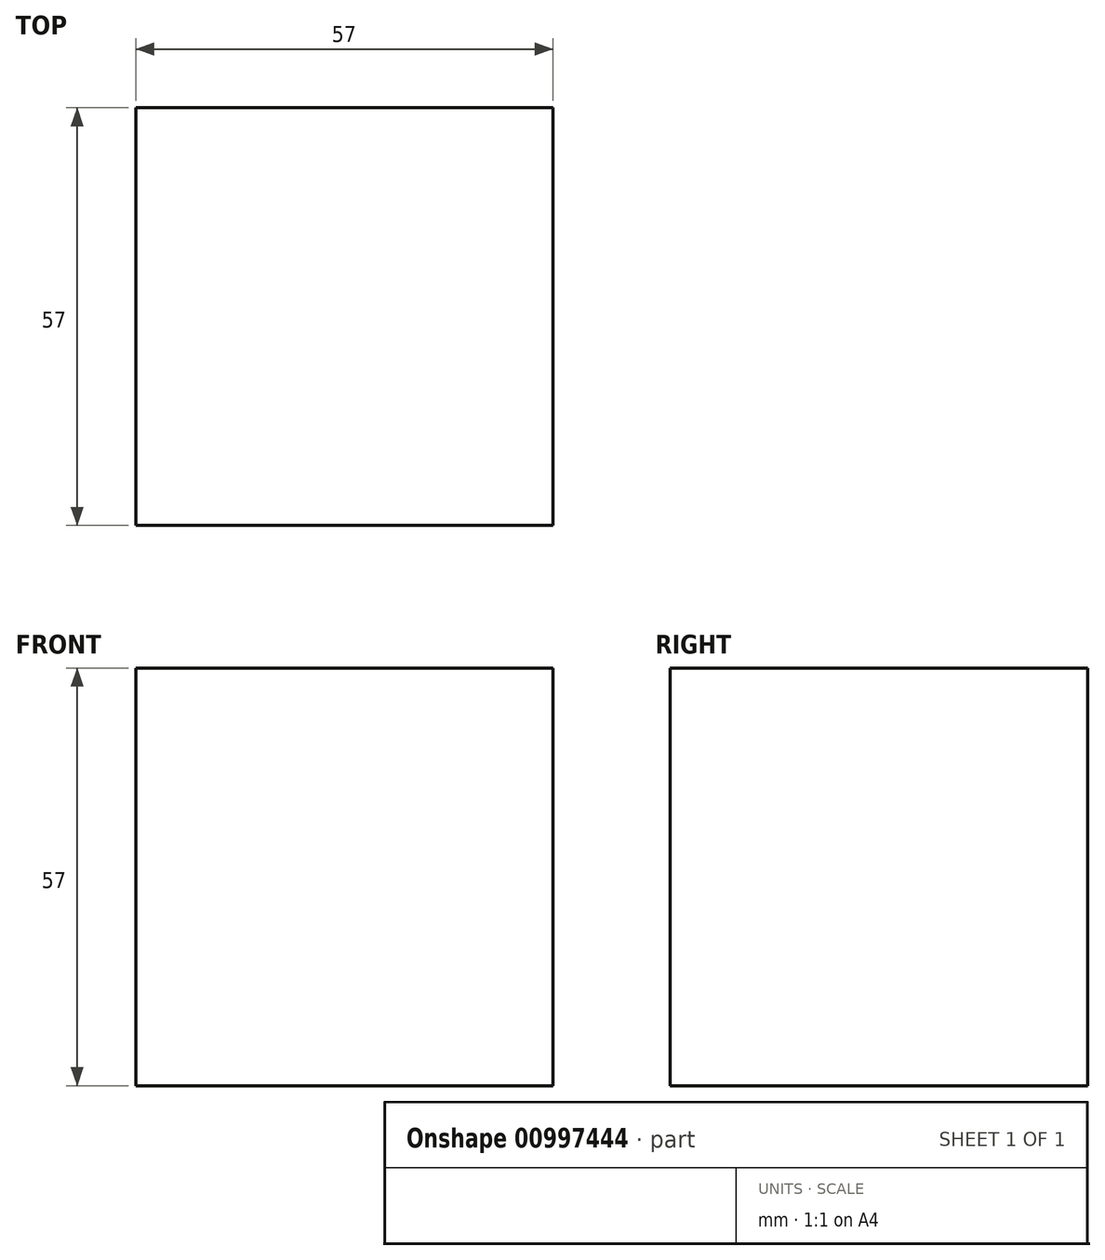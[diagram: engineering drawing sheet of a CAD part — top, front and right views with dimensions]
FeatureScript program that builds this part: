
annotation { "Feature Type Name" : "Feature", "Feature Type Description" : "" }
export const myFeature = defineFeature(function(context is Context, id is Id, definition is map)
    precondition{}
    {
        {
            var Q0;
            Q0=qCreatedBy(makeId("Front.planeOp"),FACE);
            var sketch = newSketch(context, id + "F0", { "sketchPlane" : qUnion([Q0])});
            skLineSegment(sketch, "E0.bottom", {"start": v(28.5, 28.5) * mm, "end": v(-28.5, 28.5) * mm});
            skLineSegment(sketch, "E0.top", {"start": v(28.5, -28.5) * mm, "end": v(-28.5, -28.5) * mm});
            skLineSegment(sketch, "E0.left", {"start": v(28.5, 28.5) * mm, "end": v(28.5, -28.5) * mm});
            skLineSegment(sketch, "E0.right", {"start": v(-28.5, 28.5) * mm, "end": v(-28.5, -28.5) * mm});
            skPoint(sketch, "E0.middle", {"position": v(0, 0) * mm});
            skSolve(sketch);
        }
        {
            var Q0;
            Q0=makeQuery(id+"F0.imprint","IMPRINT",FACE,{"disambiguationData":[TD([[makeQuery(id+"F0.imprint","IMPRINT",EDGE,{"derivedFrom":sQuery(id+"F0.wireOp",EDGE,"E0.bottom")}),1.0]])]});
            extrude(context, id + "F1", {"entities" : qUnion([Q0]), "endBound" : BoundingType.SYMMETRIC, "depth" : 57 * mm, "offsetDistance" : 25 * mm});
        }
    });
